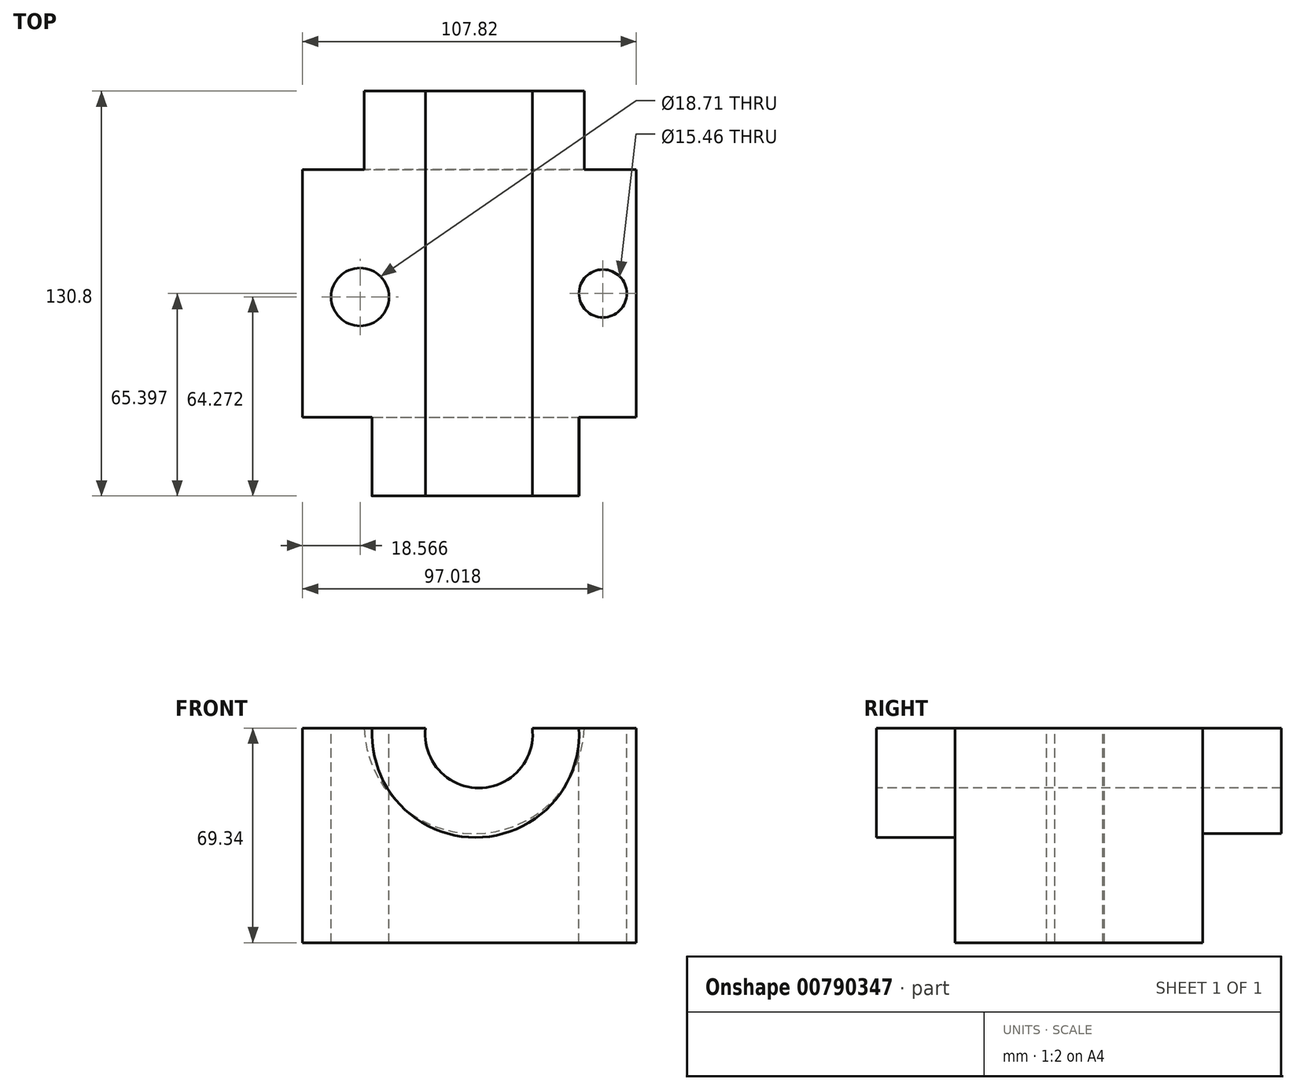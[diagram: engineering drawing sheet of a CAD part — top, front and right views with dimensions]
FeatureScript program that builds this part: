
annotation { "Feature Type Name" : "Feature", "Feature Type Description" : "" }
export const myFeature = defineFeature(function(context is Context, id is Id, definition is map)
    precondition{}
    {
        {
            var Q0;
            Q0=qCreatedBy(makeId("Top.planeOp"),FACE);
            var sketch = newSketch(context, id + "F0", { "sketchPlane" : qUnion([Q0])});
            skLineSegment(sketch, "E0.bottom", {"start": v(-54.53, 33.6) * mm, "end": v(53.3, 33.6) * mm});
            skLineSegment(sketch, "E0.top", {"start": v(-54.53, -46.4) * mm, "end": v(53.3, -46.4) * mm});
            skLineSegment(sketch, "E0.left", {"start": v(-54.53, 33.6) * mm, "end": v(-54.53, -46.4) * mm});
            skLineSegment(sketch, "E0.right", {"start": v(53.3, 33.6) * mm, "end": v(53.3, -46.4) * mm});
            skSolve(sketch);
        }
        {
            var Q0;
            Q0=makeQuery(id+"F0.imprint","IMPRINT",FACE,{"disambiguationData":[TD([[makeQuery(id+"F0.imprint","IMPRINT",EDGE,{"derivedFrom":sQuery(id+"F0.wireOp",EDGE,"E0.bottom")}),-1.0]])]});
            extrude(context, id + "F1", {"entities" : qUnion([Q0]), "depth" : 69.34 * mm, "offsetDistance" : 25.4 * mm});
        }
        {
            var Q0;
            Q0=makeQuery(id+"F1.opExtrude","SWEPT_FACE",FACE,{"disambiguationData":[OSD([sQuery(id+"F0.wireOp",EDGE,"E0.top")])]});
            var sketch = newSketch(context, id + "F2", { "sketchPlane" : qUnion([Q0])});
            skArc(sketch, "E1", {"start": v(-32.06, 69.34) * mm, "mid": v(1.35, 34) * mm, "end": v(34.76, 69.34) * mm});
            skArc(sketch, "E2", {"start": v(-14.81, 69.34) * mm, "mid": v(2.43, 49.98) * mm, "end": v(19.67, 69.34) * mm});
            skSolve(sketch);
        }
        {
            var Q0;
            {var subQ0=sQuery(id+"F2.wireOp",EDGE,"E2");Q0=makeQuery(id+"F2.imprint","IMPRINT",FACE,{"disambiguationData":[TD([[makeQuery(id+"F2.imprint","IMPRINT",EDGE,{"derivedFrom":subQ0}),1.0]])]});}
            extrude(context, id + "F3", {"entities" : qUnion([Q0]), "operationType" : NewBodyOperationType.REMOVE, "oppositeDirection" : true, "depth" : 171.7 * mm, "offsetDistance" : 25.4 * mm});
        }
        {
            var Q0;
            {var subQ0=sQuery(id+"F2.wireOp",EDGE,"E1");Q0=makeQuery(id+"F2.imprint","IMPRINT",FACE,{"disambiguationData":[TD([[makeQuery(id+"F2.imprint","IMPRINT",EDGE,{"derivedFrom":subQ0}),1.0]])]});}
            extrude(context, id + "F4", {"entities" : qUnion([Q0]), "operationType" : NewBodyOperationType.ADD, "depth" : 25.4 * mm, "offsetDistance" : 25.4 * mm});
        }
        {
            var Q0;
            Q0=makeQuery(id+"F1.opExtrude","SWEPT_FACE",FACE,{"disambiguationData":[OSD([sQuery(id+"F0.wireOp",EDGE,"E0.bottom")])]});
            var sketch = newSketch(context, id + "F5", { "sketchPlane" : qUnion([Q0])});
            skArc(sketch, "E3", {"start": v(-36.48, 69.34) * mm, "mid": v(-0.9, 35.2) * mm, "end": v(34.67, 69.34) * mm});
            skSolve(sketch);
        }
        {
            var Q0;
            {var subQ0=sQuery(id+"F5.wireOp",EDGE,"E3");Q0=makeQuery(id+"F5.imprint","IMPRINT",FACE,{"disambiguationData":[TD([[makeQuery(id+"F5.imprint","IMPRINT",EDGE,{"derivedFrom":subQ0}),1.0]])]});}
            extrude(context, id + "F6", {"entities" : qUnion([Q0]), "operationType" : NewBodyOperationType.ADD, "depth" : 25.4 * mm, "offsetDistance" : 25.4 * mm});
        }
        {
            var Q0;
            {var subQ0=sQuery(id+"F0.wireOp",EDGE,"E0.bottom");var subQ2=sQuery(id+"F0.wireOp",EDGE,"E0.right");var subQ3=makeQuery(id+"F1.opExtrude","SWEPT_FACE",FACE,{"disambiguationData":[OSD([subQ2])]});var subQ4=sQuery(id+"F0.wireOp",EDGE,"E0.top");var subQ5=makeQuery(id+"F1.opExtrude","CAP_FACE",FACE,{"disambiguationData":[OSD([subQ0,subQ4,sQuery(id+"F0.wireOp",EDGE,"E0.left"),subQ2])],"isStart":false});var subQ8=makeQuery(id+"F3.boolean.opBoolean","SPLIT",EDGE,{"disambiguationData":[TD([subQ3])],"derivedFrom":makeQuery(id+"F1.opExtrude","CAP_EDGE",EDGE,{"disambiguationData":[OSD([subQ0])],"isStart":false})});var subQ9=makeQuery(id+"F1.opExtrude","CAP_EDGE",EDGE,{"disambiguationData":[OSD([subQ4])],"isStart":false});Q0=makeQuery(id+"F6.boolean.opBoolean","MERGE",FACE,{"derivedFrom":[makeQuery(id+"F4.boolean.opBoolean","MERGE",FACE,{"derivedFrom":[makeQuery(id+"F3.boolean.opBoolean","SPLIT",FACE,{"disambiguationData":[TD([subQ3])],"derivedFrom":subQ5}),makeQuery(id+"F4.opExtrude","SWEPT_FACE",FACE,{"disambiguationData":[OSD([subQ4]),TDD([makeQuery(id+"F2.imprint","IMPRINT",EDGE,{"disambiguationData":[TD([[makeQuery(id+"F2.imprint","INTERSECT",VERTEX,{"disambiguationData":[OD(1.0)],"derivedFrom":[subQ9,sQuery(id+"F2.wireOp",EDGE,"E1")]}),1.0]])],"derivedFrom":subQ9})])]})]}),makeQuery(id+"F6.opExtrude","SWEPT_FACE",FACE,{"disambiguationData":[OSD([subQ0]),TDD([makeQuery(id+"F5.imprint","IMPRINT",EDGE,{"disambiguationData":[TD([[makeQuery(id+"F5.imprint","INTERSECT",VERTEX,{"derivedFrom":[subQ8,sQuery(id+"F5.wireOp",EDGE,"E3")]}),1.0]])],"derivedFrom":subQ8})])]})]});}
            var sketch = newSketch(context, id + "F7", { "sketchPlane" : qUnion([Q0])});
            skCircle(sketch, "E4", {"center": v(42.49, -6.4) * mm, "radius": 7.73 * mm});
            skPoint(sketch, "E4.centerSnap0", {"position": v(19.67, -6.4) * mm});
            skCircle(sketch, "E5", {"center": v(-35.96, -7.52) * mm, "radius": 9.36 * mm});
            skSolve(sketch);
        }
        {
            var Q0;
            Q0=makeQuery(id+"F7.imprint","IMPRINT",FACE,{"disambiguationData":[TD([[makeQuery(id+"F7.imprint","IMPRINT",EDGE,{"derivedFrom":sQuery(id+"F7.wireOp",EDGE,"E5")}),1.0]])]});
            extrude(context, id + "F8", {"entities" : qUnion([Q0]), "operationType" : NewBodyOperationType.REMOVE, "oppositeDirection" : true, "depth" : 220.22 * mm, "offsetDistance" : 25.4 * mm});
        }
        {
            var Q0;
            Q0=makeQuery(id+"F7.imprint","IMPRINT",FACE,{"disambiguationData":[TD([[makeQuery(id+"F7.imprint","IMPRINT",EDGE,{"derivedFrom":sQuery(id+"F7.wireOp",EDGE,"E4")}),1.0]])]});
            extrude(context, id + "F9", {"entities" : qUnion([Q0]), "operationType" : NewBodyOperationType.REMOVE, "oppositeDirection" : true, "depth" : 194.3 * mm, "offsetDistance" : 25.4 * mm});
        }
    });
